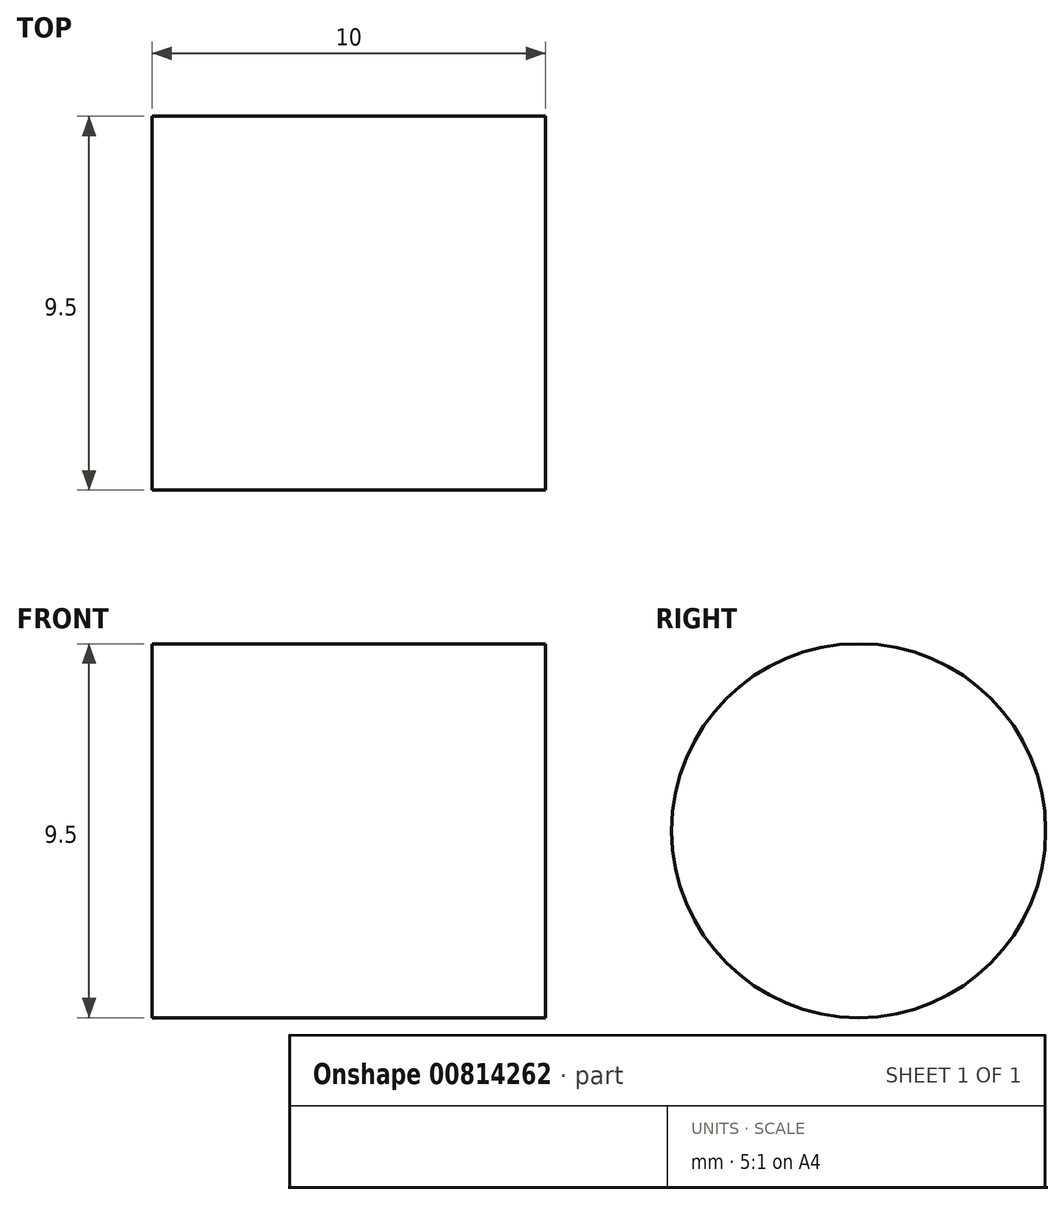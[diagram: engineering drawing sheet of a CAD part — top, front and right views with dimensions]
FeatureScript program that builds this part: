
annotation { "Feature Type Name" : "Feature", "Feature Type Description" : "" }
export const myFeature = defineFeature(function(context is Context, id is Id, definition is map)
    precondition{}
    {
        {
            var Q0;
            Q0=qCreatedBy(makeId("Right.planeOp"),FACE);
            var sketch = newSketch(context, id + "F0", { "sketchPlane" : qUnion([Q0])});
            skCircle(sketch, "E0", {"center": v(0, 0) * mm, "radius": 4.75 * mm});
            skSolve(sketch);
        }
        {
            var Q0;
            Q0=makeQuery(id+"F0.imprint","IMPRINT",FACE,{"disambiguationData":[TD([[makeQuery(id+"F0.imprint","IMPRINT",EDGE,{"derivedFrom":sQuery(id+"F0.wireOp",EDGE,"E0")}),1.0]])]});
            var Q1;
            Q1=sQuery(id+"F0.wireOp",EDGE,"E0");
            extrude(context, id + "F1", {"entities" : qUnion([Q0]), "surfaceEntities" : qUnion([Q1]), "depth" : 10 * mm, "offsetDistance" : 25 * mm});
        }
    });
